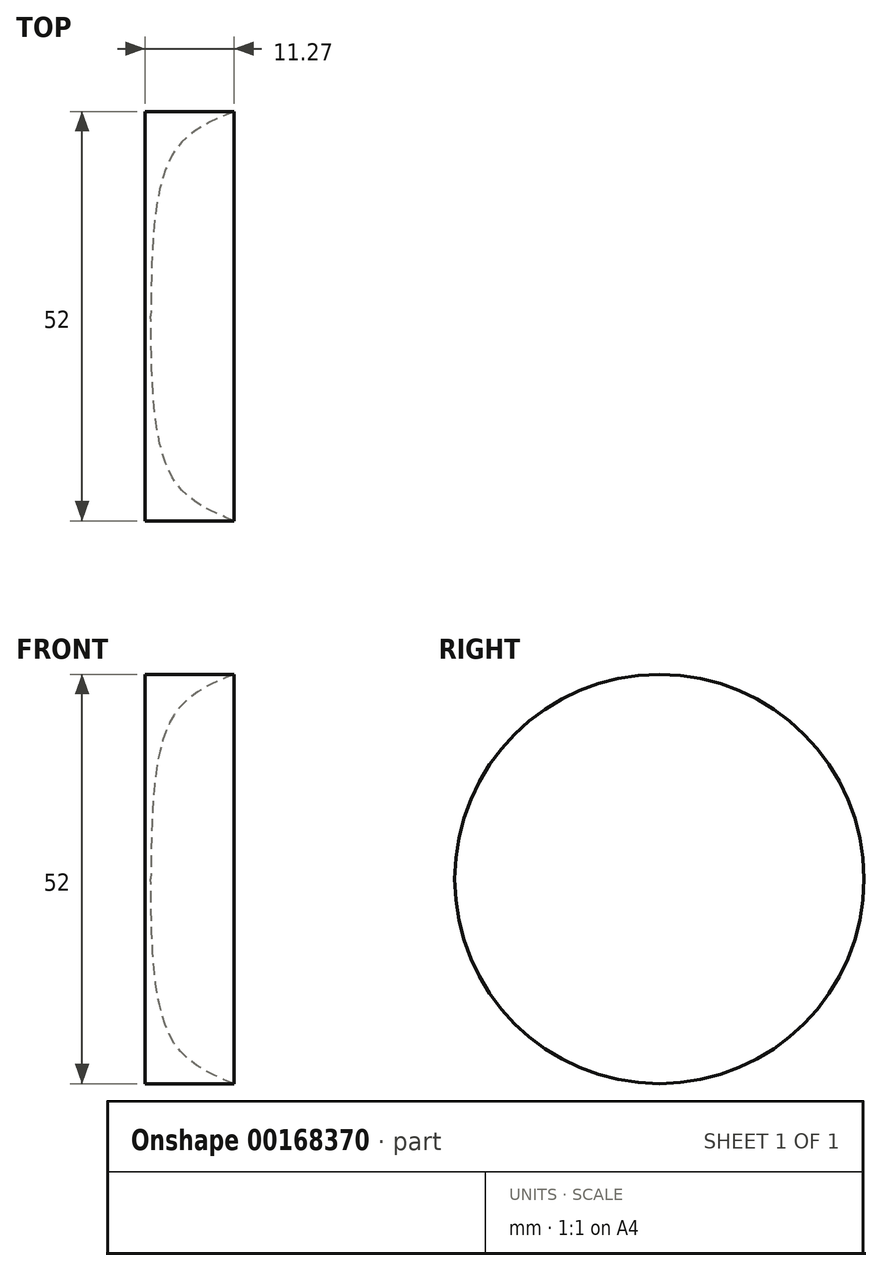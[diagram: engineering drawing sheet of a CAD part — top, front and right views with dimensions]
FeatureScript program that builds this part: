
annotation { "Feature Type Name" : "Feature", "Feature Type Description" : "" }
export const myFeature = defineFeature(function(context is Context, id is Id, definition is map)
    precondition{}
    {
        {
            var Q0;
            Q0=qCreatedBy(makeId("Front.planeOp"),FACE);
            var sketch = newSketch(context, id + "F0", { "sketchPlane" : qUnion([Q0])});
            skLineSegment(sketch, "E0", {"start": v(0, 0) * mm, "end": v(0, 26) * mm});
            skLineSegment(sketch, "E1", {"start": v(0, 26) * mm, "end": v(11.27, 26) * mm});
            skFitSpline(sketch, "E2", {"points": [v(11.27, 26) * mm, v(3.56, 20.62) * mm, v(0.72, 0) * mm], "startDerivative": vector(-22.1, -9.14) * mm, "endDerivative": vector(-0.41, -40.8) * mm});
            skLineSegment(sketch, "E3", {"start": v(0, 0) * mm, "end": v(0.72, 0) * mm});
            skSolve(sketch);
        }
        {
            var Q0;
            Q0=makeQuery(id+"F0.imprint","IMPRINT",FACE,{"disambiguationData":[TD([[makeQuery(id+"F0.imprint","IMPRINT",EDGE,{"derivedFrom":sQuery(id+"F0.wireOp",EDGE,"E0")}),-1.0]])]});
            var Q1;
            Q1=sQuery(id+"F0.wireOp",EDGE,"E3");
            revolve(context, id + "F1", {"entities" : qUnion([Q0]), "axis" : qUnion([Q1]), "revolveType" : RevolveType.FULL});
        }
    });
